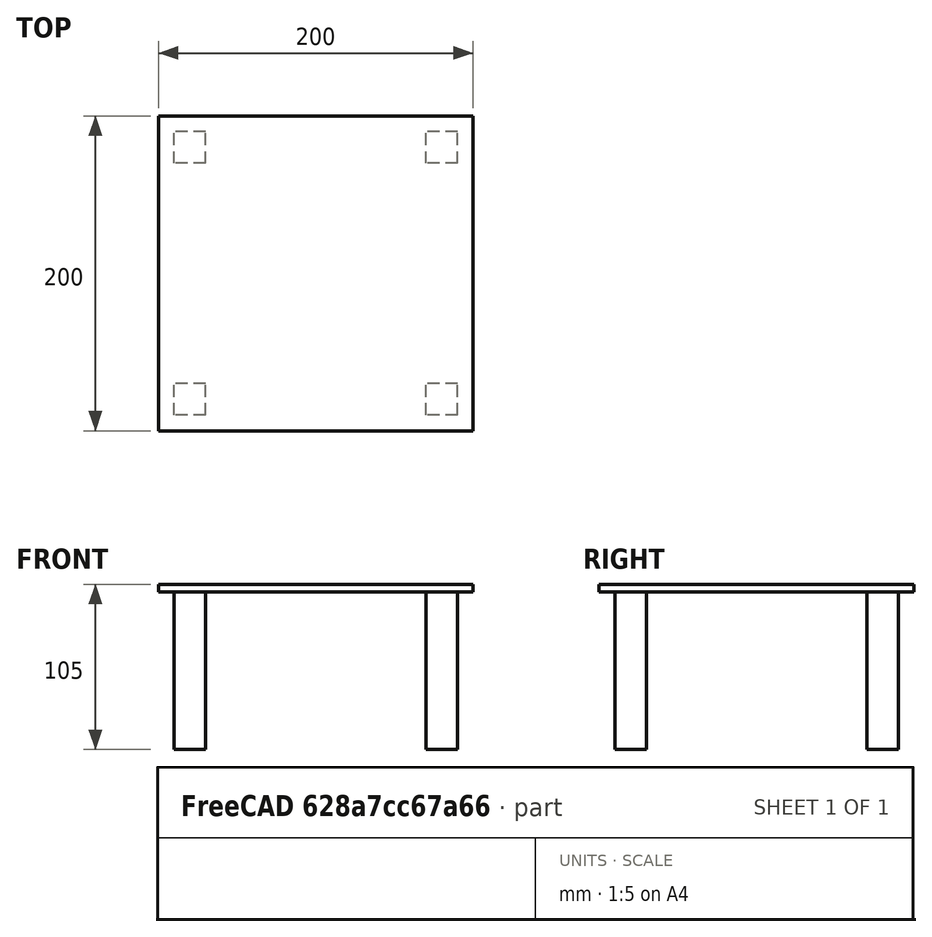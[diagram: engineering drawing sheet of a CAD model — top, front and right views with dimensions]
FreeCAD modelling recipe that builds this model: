
FCSTD DOCUMENT  (FreeCAD 0.20R29177 +426 (Git))
Label: Ejemplo 1
License: All rights reserved
LicenseURL: http://en.wikipedia.org/wiki/All_rights_reserved
objects: Part::Box×5, Part::MultiFuse×1
note: 6 computed .brp shape members not serialized (recipe doc carries the construction recipe); baked Part::Feature solids carry a one-line shape summary decoded from their .brp

FEATURE [Part::Box] Box  label="Plancha mesa"
  AttacherType = Attacher::AttachEngine3D
  Height = 5
  Length = 200
  Width = 200
FEATURE [Part::Box] Box001  label="Pata1"
  AttacherType = Attacher::AttachEngine3D
  Height = 101
  Length = 20
  Placement = pos=(10,10,-100) rot=(0,0,1;0rad)
  Width = 20
FEATURE [Part::Box] Box002  label="Pata 2"
  AttacherType = Attacher::AttachEngine3D
  Height = 101
  Length = 20
  Placement = pos=(170,10,-100) rot=(0,0,1;0rad)
  Width = 20
FEATURE [Part::Box] Box003  label="Pata 3"
  AttacherType = Attacher::AttachEngine3D
  Height = 101
  Length = 20
  Placement = pos=(10,170,-100) rot=(0,0,1;0rad)
  Width = 20
FEATURE [Part::Box] Box004  label="Pata 4"
  AttacherType = Attacher::AttachEngine3D
  Height = 101
  Length = 20
  Placement = pos=(170,170,-100) rot=(0,0,1;0rad)
  Width = 20
FEATURE [Part::MultiFuse] Fusion  label="Mesa"
  Shapes = -> [Box,Box001,Box002,Box003,Box004]
